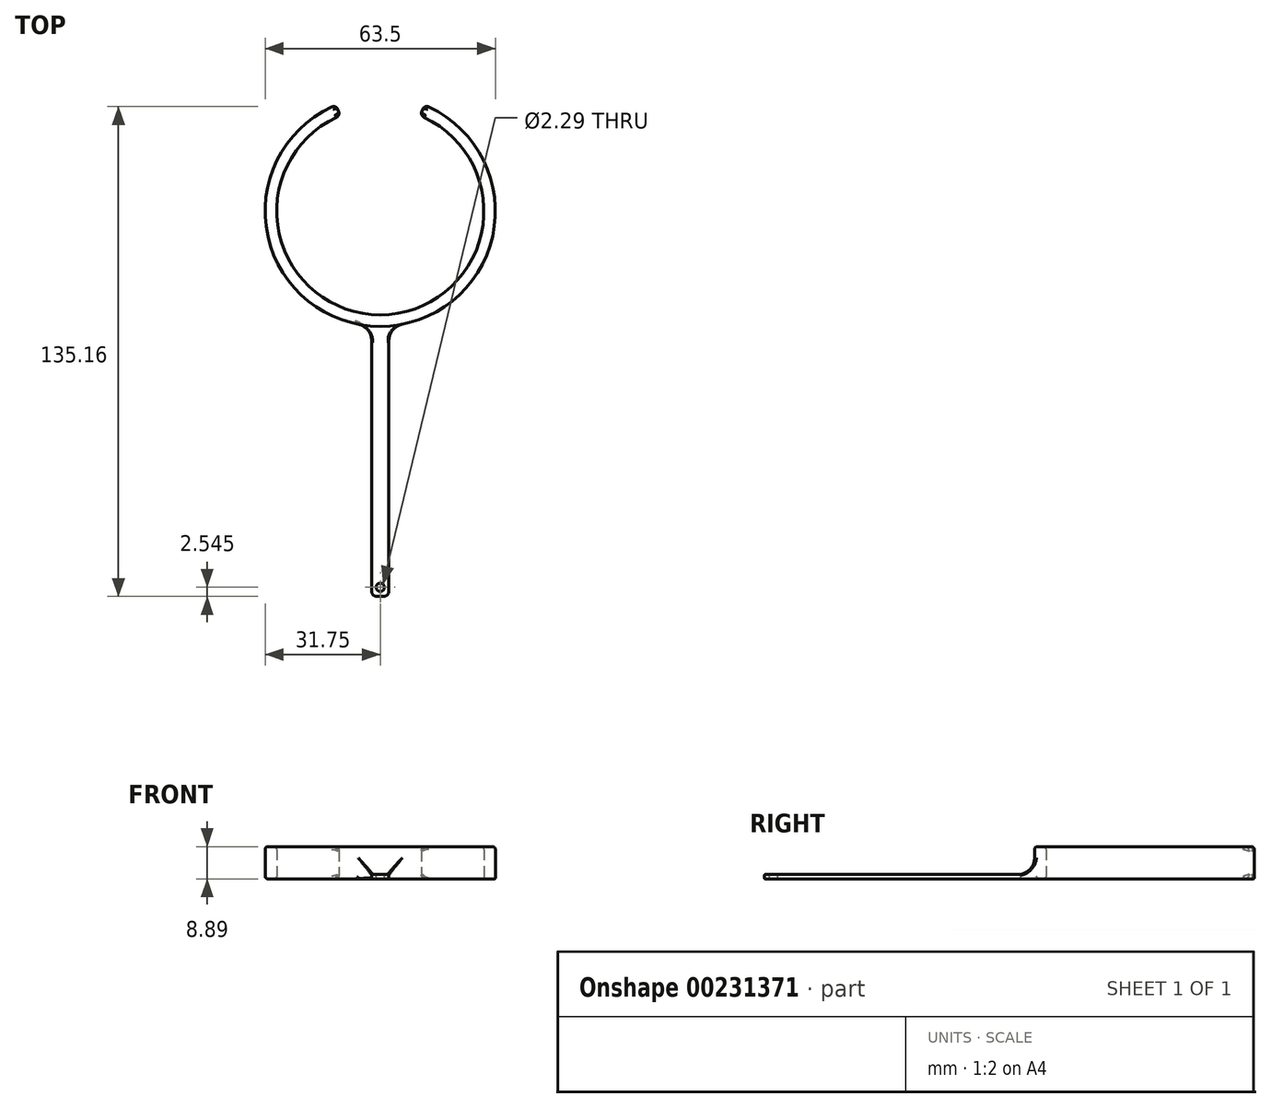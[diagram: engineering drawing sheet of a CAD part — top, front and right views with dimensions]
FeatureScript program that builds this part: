
annotation { "Feature Type Name" : "Feature", "Feature Type Description" : "" }
export const myFeature = defineFeature(function(context is Context, id is Id, definition is map)
    precondition{}
    {
        {
            var Q0;
            Q0=qCreatedBy(makeId("Top.planeOp"),FACE);
            var sketch = newSketch(context, id + "F0", { "sketchPlane" : qUnion([Q0])});
            skArc(sketch, "E0", {"start": v(-11, 26.38) * mm, "mid": v(0, -28.57) * mm, "end": v(11, 26.38) * mm});
            skArc(sketch, "E1", {"start": v(-12.21, 29.3) * mm, "mid": v(0, -31.75) * mm, "end": v(12.21, 29.3) * mm});
            skLineSegment(sketch, "E2", {"start": v(-11, 26.38) * mm, "end": v(-12.21, 29.3) * mm});
            skLineSegment(sketch, "E3", {"start": v(12.21, 29.3) * mm, "end": v(11, 26.38) * mm});
            skSolve(sketch);
        }
        {
            var Q0;
            Q0 = qSketchRegion(id + "F0", true);
            extrude(context, id + "F1", {"entities" : qUnion([Q0]), "depth" : 8.9 * mm});
        }
        {
            var Q0;
            Q0=qCreatedBy(makeId("Top.planeOp"),FACE);
            var sketch = newSketch(context, id + "F2", { "sketchPlane" : qUnion([Q0])});
            skLineSegment(sketch, "E4.bottom", {"start": v(-2.4, -30.07) * mm, "end": v(2.4, -30.07) * mm});
            skLineSegment(sketch, "E4.top", {"start": v(-2.4, -106.27) * mm, "end": v(2.4, -106.27) * mm});
            skLineSegment(sketch, "E4.left", {"start": v(-2.4, -30.07) * mm, "end": v(-2.4, -106.27) * mm});
            skLineSegment(sketch, "E4.right", {"start": v(2.4, -30.07) * mm, "end": v(2.4, -106.27) * mm});
            skSolve(sketch);
        }
        {
            var Q0;
            Q0 = qSketchRegion(id + "F2", true);
            extrude(context, id + "F3", {"entities" : qUnion([Q0]), "operationType" : NewBodyOperationType.ADD, "depth" : 1.2 * mm});
        }
        {
            var Q0;
            Q0=makeQuery(id+"F3.opExtrude","CAP_FACE",FACE,{"disambiguationData":[OSD([sQuery(id+"F2.wireOp",EDGE,"E4.bottom"),sQuery(id+"F2.wireOp",EDGE,"E4.top"),sQuery(id+"F2.wireOp",EDGE,"E4.left"),sQuery(id+"F2.wireOp",EDGE,"E4.right")])],"isStart":false});
            var sketch = newSketch(context, id + "F4", { "sketchPlane" : qUnion([Q0])});
            skCircle(sketch, "E5", {"center": v(0, -103.73) * mm, "radius": 1.14 * mm});
            skPoint(sketch, "E5.centerSnap0", {"position": v(0, -106.27) * mm});
            skSolve(sketch);
        }
        {
            var Q0;
            Q0 = qSketchRegion(id + "F4", true);
            extrude(context, id + "F5", {"entities" : qUnion([Q0]), "operationType" : NewBodyOperationType.REMOVE, "oppositeDirection" : true, "depth" : 25.4 * mm});
        }
        {
            var Q0;
            Q0=makeQuery(id+"F3.opExtrude","SWEPT_EDGE",EDGE,{"disambiguationData":[OSD([sQuery(id+"F2.wireOp",EDGE,"E4.top"),sQuery(id+"F2.wireOp",EDGE,"E4.left")])]});
            var Q1;
            Q1=makeQuery(id+"F3.opExtrude","SWEPT_EDGE",EDGE,{"disambiguationData":[OSD([sQuery(id+"F2.wireOp",EDGE,"E4.top"),sQuery(id+"F2.wireOp",EDGE,"E4.right")])]});
            fillet(context, id + "F6", {"entities" : qUnion([Q0, Q1]), "radius" : 1.52 * mm, "tangentPropagation" : true, "allowEdgeOverflow" : false});
        }
        {
            var Q0;
            Q0=makeQuery(id+"F1.opExtrude","CAP_EDGE",EDGE,{"disambiguationData":[OSD([sQuery(id+"F0.wireOp",EDGE,"E0")])],"isStart":true});
            var Q1;
            Q1=makeQuery(id+"F1.opExtrude","CAP_EDGE",EDGE,{"disambiguationData":[OSD([sQuery(id+"F0.wireOp",EDGE,"E0")])],"isStart":false});
            var Q2;
            Q2=makeQuery(id+"F1.opExtrude","CAP_EDGE",EDGE,{"disambiguationData":[OSD([sQuery(id+"F0.wireOp",EDGE,"E1")])],"isStart":false});
            var Q3;
            {var subQ0=sQuery(id+"F0.wireOp",EDGE,"E2");var subQ2=sQuery(id+"F0.wireOp",EDGE,"E1");Q3=makeQuery(id+"F3.boolean.opBoolean","SPLIT",EDGE,{"disambiguationData":[TD([makeQuery(id+"F1.opExtrude","SWEPT_FACE",FACE,{"disambiguationData":[OSD([subQ0])]})])],"derivedFrom":makeQuery(id+"F1.opExtrude","CAP_EDGE",EDGE,{"disambiguationData":[OSD([subQ2])],"isStart":true})});}
            fillet(context, id + "F7", {"entities" : qUnion([Q0, Q1, Q2, Q3]), "radius" : 0.76 * mm, "tangentPropagation" : true, "allowEdgeOverflow" : false});
        }
        {
            var Q0;
            Q0=makeQuery(id+"F3.boolean.opBoolean","INTERSECT",EDGE,{"derivedFrom":[makeQuery(id+"F1.opExtrude","SWEPT_FACE",FACE,{"disambiguationData":[OSD([sQuery(id+"F0.wireOp",EDGE,"E1")])]}),makeQuery(id+"F3.opExtrude","CAP_FACE",FACE,{"disambiguationData":[OSD([sQuery(id+"F2.wireOp",EDGE,"E4.bottom"),sQuery(id+"F2.wireOp",EDGE,"E4.top"),sQuery(id+"F2.wireOp",EDGE,"E4.left"),sQuery(id+"F2.wireOp",EDGE,"E4.right")])],"isStart":false})]});
            var Q1;
            Q1=makeQuery(id+"F3.boolean.opBoolean","INTERSECT",EDGE,{"derivedFrom":[makeQuery(id+"F1.opExtrude","SWEPT_FACE",FACE,{"disambiguationData":[OSD([sQuery(id+"F0.wireOp",EDGE,"E1")])]}),makeQuery(id+"F3.opExtrude","SWEPT_FACE",FACE,{"disambiguationData":[OSD([sQuery(id+"F2.wireOp",EDGE,"E4.right")])]})]});
            var Q2;
            Q2=makeQuery(id+"F3.boolean.opBoolean","INTERSECT",EDGE,{"derivedFrom":[makeQuery(id+"F1.opExtrude","SWEPT_FACE",FACE,{"disambiguationData":[OSD([sQuery(id+"F0.wireOp",EDGE,"E1")])]}),makeQuery(id+"F3.opExtrude","SWEPT_FACE",FACE,{"disambiguationData":[OSD([sQuery(id+"F2.wireOp",EDGE,"E4.left")])]})]});
            fillet(context, id + "F8", {"entities" : qUnion([Q0, Q1, Q2]), "radius" : 4.57 * mm, "tangentPropagation" : true, "allowEdgeOverflow" : false});
        }
        {
            var Q0;
            Q0=makeQuery(id+"F3.opExtrude","CAP_EDGE",EDGE,{"disambiguationData":[OSD([sQuery(id+"F2.wireOp",EDGE,"E4.right")])],"isStart":false});
            var Q1;
            Q1=makeQuery(id+"F3.opExtrude","CAP_EDGE",EDGE,{"disambiguationData":[OSD([sQuery(id+"F2.wireOp",EDGE,"E4.right")])],"isStart":true});
            fillet(context, id + "F9", {"entities" : qUnion([Q0, Q1]), "radius" : 0.25 * mm, "tangentPropagation" : true, "allowEdgeOverflow" : false});
        }
        {
            var Q0;
            Q0=makeQuery(id+"F1.opExtrude","SWEPT_EDGE",EDGE,{"disambiguationData":[OSD([sQuery(id+"F0.wireOp",EDGE,"E1"),sQuery(id+"F0.wireOp",EDGE,"E2")])]});
            var Q1;
            Q1=makeQuery(id+"F1.opExtrude","SWEPT_EDGE",EDGE,{"disambiguationData":[OSD([sQuery(id+"F0.wireOp",EDGE,"E1"),sQuery(id+"F0.wireOp",EDGE,"E3")])]});
            fillet(context, id + "F10", {"entities" : qUnion([Q0, Q1]), "radius" : 1.27 * mm, "tangentPropagation" : true, "allowEdgeOverflow" : false});
        }
    });
